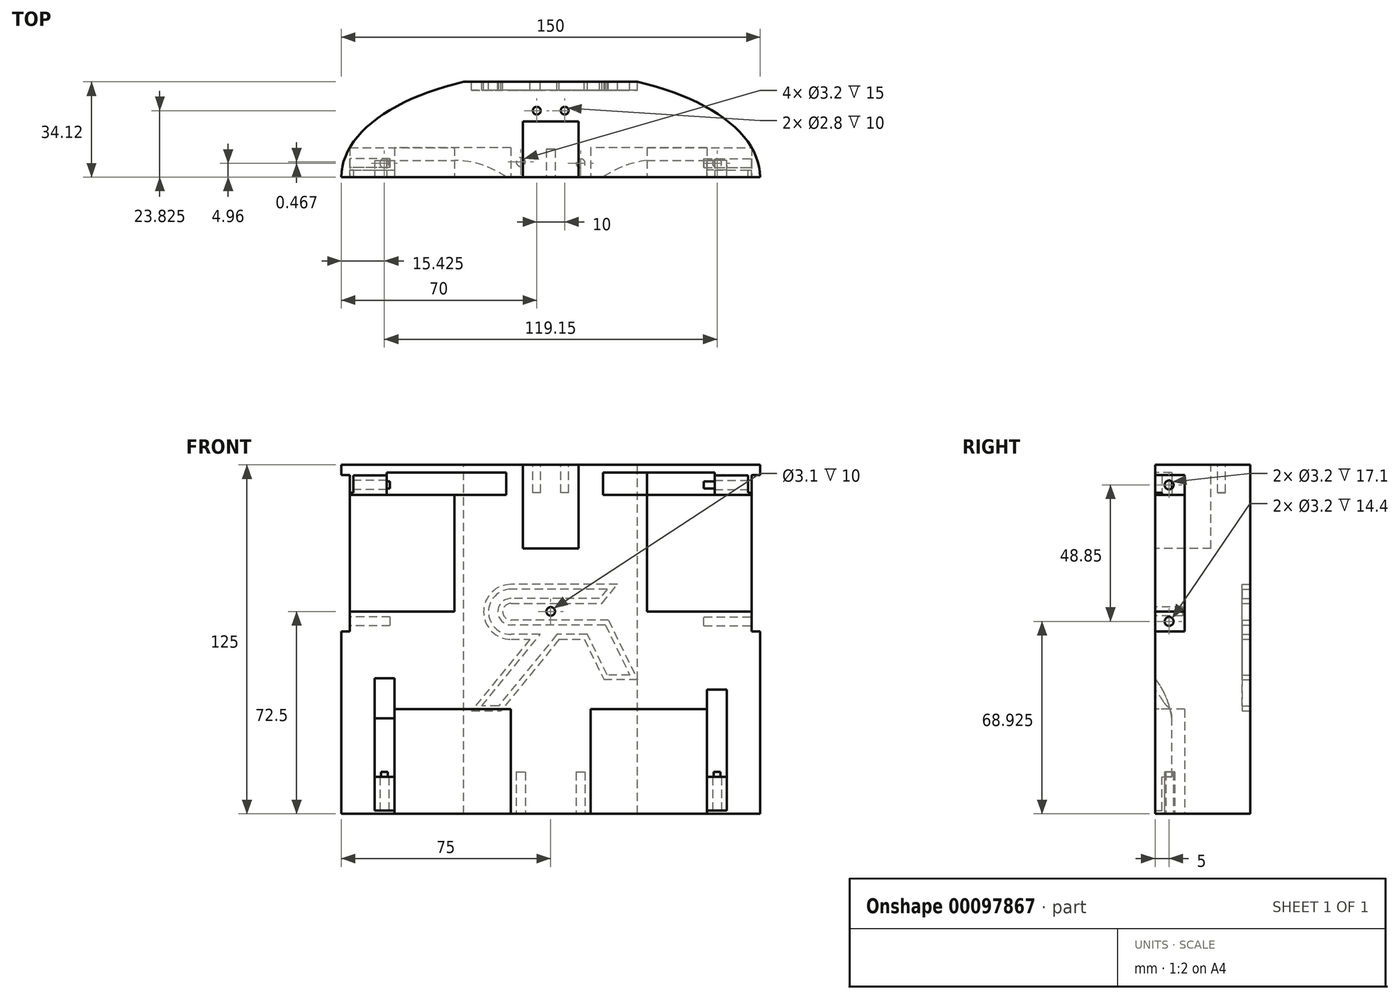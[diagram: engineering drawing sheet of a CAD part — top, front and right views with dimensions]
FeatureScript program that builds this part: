
annotation { "Feature Type Name" : "Feature", "Feature Type Description" : "" }
export const myFeature = defineFeature(function(context is Context, id is Id, definition is map)
    precondition{}
    {
        {
            var Q0;
            Q0=qCreatedBy(makeId("Top.planeOp"),FACE);
            var sketch = newSketch(context, id + "F0", { "sketchPlane" : qUnion([Q0])});
            skLineSegment(sketch, "E0.bottom", {"start": v(-150, 0) * mm, "end": v(0, 0) * mm});
            skLineSegment(sketch, "E0.top", {"start": v(-150, -75) * mm, "end": v(0, -75) * mm});
            skLineSegment(sketch, "E0.left", {"start": v(-150, 0) * mm, "end": v(-150, -75) * mm});
            skLineSegment(sketch, "E0.right", {"start": v(0, 0) * mm, "end": v(0, -75) * mm});
            skLineSegment(sketch, "E1", {"start": v(0, -37.5) * mm, "end": v(-150, -37.5) * mm});
            skPoint(sketch, "E2", {"position": v(-75, -37.5) * mm});
            skEllipse(sketch, "E3", {"center": v(-75, -37.5) * mm, "majorRadius": 75 * mm, "minorRadius": 37.5 * mm, "majorAxis": v(1, 0)});
            skSolve(sketch);
        }
        {
            var Q0;
            {var subQ0=sQuery(id+"F0.wireOp",EDGE,"E1");Q0=makeQuery(id+"F0.imprint","IMPRINT",FACE,{"disambiguationData":[TD([[makeQuery(id+"F0.imprint","IMPRINT",EDGE,{"derivedFrom":subQ0}),1.0]])]});}
            var Q1;
            {var subQ0=sQuery(id+"F0.wireOp",EDGE,"E1");Q1=makeQuery(id+"F0.imprint","IMPRINT",FACE,{"disambiguationData":[TD([[makeQuery(id+"F0.imprint","IMPRINT",EDGE,{"derivedFrom":subQ0}),-1.0]])]});}
            extrude(context, id + "F1", {"entities" : qUnion([Q0, Q1]), "depth" : 125 * mm});
        }
        {
            var Q0;
            Q0=qCreatedBy(makeId("Right.planeOp"),FACE);
            var sketch = newSketch(context, id + "F2", { "sketchPlane" : qUnion([Q0])});
            skLineSegment(sketch, "E4.bottom", {"start": v(-48.1, 114.2) * mm, "end": v(-26.9, 114.2) * mm});
            skLineSegment(sketch, "E4.top", {"start": v(-48.1, 72.5) * mm, "end": v(-26.9, 72.5) * mm});
            skLineSegment(sketch, "E4.left", {"start": v(-48.1, 114.2) * mm, "end": v(-48.1, 72.5) * mm});
            skLineSegment(sketch, "E4.right", {"start": v(-26.9, 114.2) * mm, "end": v(-26.9, 72.5) * mm});
            skPoint(sketch, "E5", {"position": v(-37.5, 125) * mm});
            skPoint(sketch, "E6", {"position": v(-37.5, 114.2) * mm});
            skLineSegment(sketch, "E7", {"start": v(-37.5, 125) * mm, "end": v(-37.5, 121.35) * mm});
            skLineSegment(sketch, "E8.bottom", {"start": v(-48.1, 113.35) * mm, "end": v(-26.9, 113.35) * mm, "construction": true});
            skLineSegment(sketch, "E8.top", {"start": v(-48.1, 73.35) * mm, "end": v(-26.9, 73.35) * mm, "construction": true});
            skLineSegment(sketch, "E8.left", {"start": v(-48.1, 113.35) * mm, "end": v(-48.1, 73.35) * mm, "construction": true});
            skLineSegment(sketch, "E8.right", {"start": v(-26.9, 113.35) * mm, "end": v(-26.9, 73.35) * mm, "construction": true});
            skPoint(sketch, "E9", {"position": v(-26.9, 93.35) * mm});
            skLineSegment(sketch, "E10.bottom", {"start": v(-48.1, 113.35) * mm, "end": v(-26.9, 113.35) * mm});
            skLineSegment(sketch, "E10.top", {"start": v(-48.1, 121.35) * mm, "end": v(-26.9, 121.35) * mm});
            skLineSegment(sketch, "E10.left", {"start": v(-48.1, 113.35) * mm, "end": v(-48.1, 121.35) * mm});
            skLineSegment(sketch, "E10.right", {"start": v(-26.9, 113.35) * mm, "end": v(-26.9, 121.35) * mm});
            skLineSegment(sketch, "E11.bottom", {"start": v(-48.1, 73.35) * mm, "end": v(-26.9, 73.35) * mm});
            skLineSegment(sketch, "E11.top", {"start": v(-48.1, 65.35) * mm, "end": v(-26.9, 65.35) * mm});
            skLineSegment(sketch, "E11.left", {"start": v(-48.1, 73.35) * mm, "end": v(-48.1, 65.35) * mm});
            skLineSegment(sketch, "E11.right", {"start": v(-26.9, 73.35) * mm, "end": v(-26.9, 65.35) * mm});
            skLineSegment(sketch, "E12", {"start": v(-37.5, 65.35) * mm, "end": v(-37.5, 0) * mm});
            skLineSegment(sketch, "E13", {"start": v(-37.5, 121.35) * mm, "end": v(-37.5, 125) * mm});
            skLineSegment(sketch, "E14.trimOffspring", {"start": v(-37.5, 114.2) * mm, "end": v(-37.5, 72.5) * mm});
            skSolve(sketch);
        }
        {
            var Q0;
            {var subQ0=sQuery(id+"F2.wireOp",EDGE,"E4.right");Q0=makeQuery(id+"F2.imprint","IMPRINT",FACE,{"disambiguationData":[TD([[makeQuery(id+"F2.imprint","IMPRINT",EDGE,{"derivedFrom":subQ0}),-1.0]])]});}
            var Q1;
            {var subQ0=sQuery(id+"F2.wireOp",EDGE,"E4.left");Q1=makeQuery(id+"F2.imprint","IMPRINT",FACE,{"disambiguationData":[TD([[makeQuery(id+"F2.imprint","IMPRINT",EDGE,{"derivedFrom":subQ0}),1.0]])]});}
            var Q2;
            {var subQ0=sQuery(id+"F2.wireOp",EDGE,"E11.left");var subQ1=sQuery(id+"F2.wireOp",EDGE,"E4.top");var subQ2=makeQuery(id+"F2.imprint","INTERSECT",VERTEX,{"derivedFrom":[subQ1,subQ0]});Q2=makeQuery(id+"F2.imprint","IMPRINT",FACE,{"disambiguationData":[TD([[makeQuery(id+"F2.imprint","IMPRINT",EDGE,{"disambiguationData":[TD([[subQ2,-1.0]])],"derivedFrom":subQ1}),1.0]])]});}
            var Q3;
            {var subQ0=sQuery(id+"F2.wireOp",EDGE,"E11.right");var subQ1=sQuery(id+"F2.wireOp",EDGE,"E4.top");var subQ2=makeQuery(id+"F2.imprint","INTERSECT",VERTEX,{"derivedFrom":[subQ1,subQ0]});Q3=makeQuery(id+"F2.imprint","IMPRINT",FACE,{"disambiguationData":[TD([[makeQuery(id+"F2.imprint","IMPRINT",EDGE,{"disambiguationData":[TD([[subQ2,1.0]])],"derivedFrom":subQ1}),1.0]])]});}
            var Q4;
            {var subQ0=sQuery(id+"F2.wireOp",EDGE,"E10.left");var subQ1=sQuery(id+"F2.wireOp",EDGE,"E4.bottom");var subQ2=makeQuery(id+"F2.imprint","INTERSECT",VERTEX,{"derivedFrom":[subQ1,subQ0]});Q4=makeQuery(id+"F2.imprint","IMPRINT",FACE,{"disambiguationData":[TD([[makeQuery(id+"F2.imprint","IMPRINT",EDGE,{"disambiguationData":[TD([[subQ2,-1.0]])],"derivedFrom":subQ1}),-1.0]])]});}
            var Q5;
            {var subQ0=sQuery(id+"F2.wireOp",EDGE,"E10.right");var subQ1=sQuery(id+"F2.wireOp",EDGE,"E4.bottom");var subQ2=makeQuery(id+"F2.imprint","INTERSECT",VERTEX,{"derivedFrom":[subQ1,subQ0]});Q5=makeQuery(id+"F2.imprint","IMPRINT",FACE,{"disambiguationData":[TD([[makeQuery(id+"F2.imprint","IMPRINT",EDGE,{"disambiguationData":[TD([[subQ2,1.0]])],"derivedFrom":subQ1}),-1.0]])]});}
            extrude(context, id + "F3", {"entities" : qUnion([Q0, Q1, Q2, Q3, Q4, Q5]), "operationType" : NewBodyOperationType.REMOVE, "oppositeDirection" : true, "depth" : 155.5 * mm});
        }
        {
            var Q0;
            Q0=makeQuery(id+"F3.boolean.opBoolean","COPY",FACE,{"derivedFrom":makeQuery(id+"F3.opExtrude","SWEPT_FACE",FACE,{"disambiguationData":[OSD([sQuery(id+"F2.wireOp",EDGE,"E4.top")])]})});
            var sketch = newSketch(context, id + "F4", { "sketchPlane" : qUnion([Q0])});
            skLineSegment(sketch, "E15", {"start": v(-3.06, -48.1) * mm, "end": v(-3.06, -26.9) * mm});
            skEllipticalArc(sketch, "E16.0", {});
            skLineSegment(sketch, "E17", {"start": v(-146.94, -48.1) * mm, "end": v(-146.94, -26.9) * mm});
            skEllipticalArc(sketch, "E18.0", {});
            const initialGuessF4  = {"E16.0": [-0.075, -0.0375, 1, 0, 0.075, 0.0375, 5.996612290444908, 0.28657301673467844], "E18.0": [-0.075, -0.0375, 1, 0, 0.075, 0.0375, 2.855019636855115, 3.428165670324471]};
            skSetInitialGuess(sketch, initialGuessF4);
            skSolve(sketch);
        }
        {
            var Q0;
            Q0=makeQuery(id+"F4.imprint","IMPRINT",FACE,{"disambiguationData":[TD([[makeQuery(id+"F4.imprint","IMPRINT",EDGE,{"derivedFrom":sQuery(id+"F4.wireOp",EDGE,"E17")}),1.0]])]});
            var Q1;
            Q1=makeQuery(id+"F4.imprint","IMPRINT",FACE,{"disambiguationData":[TD([[makeQuery(id+"F4.imprint","IMPRINT",EDGE,{"derivedFrom":sQuery(id+"F4.wireOp",EDGE,"E15")}),-1.0]])]});
            extrude(context, id + "F5", {"entities" : qUnion([Q0, Q1]), "operationType" : NewBodyOperationType.REMOVE, "oppositeDirection" : true, "depth" : 7.15 * mm});
        }
        {
            var Q0;
            Q0=makeQuery(id+"F3.boolean.opBoolean","COPY",FACE,{"derivedFrom":makeQuery(id+"F3.opExtrude","SWEPT_FACE",FACE,{"disambiguationData":[OSD([sQuery(id+"F2.wireOp",EDGE,"E4.bottom")])]})});
            var sketch = newSketch(context, id + "F6", { "sketchPlane" : qUnion([Q0])});
            skLineSegment(sketch, "E19", {"start": v(-3.06, 26.9) * mm, "end": v(-3.06, 48.1) * mm});
            skEllipticalArc(sketch, "E20.0", {});
            skLineSegment(sketch, "E21", {"start": v(-146.94, 26.9) * mm, "end": v(-146.94, 48.1) * mm});
            skEllipticalArc(sketch, "E22.0", {});
            const initialGuessF6  = {"E20.0": [-0.075, 0.0375, 1, 0, 0.075, 0.0375, 5.996612290444908, 0.28657301673467805], "E22.0": [-0.075, 0.0375, 1, 0, 0.075, 0.0375, 2.8550196368551153, 3.428165670324471]};
            skSetInitialGuess(sketch, initialGuessF6);
            skSolve(sketch);
        }
        {
            var Q0;
            Q0=makeQuery(id+"F6.imprint","IMPRINT",FACE,{"disambiguationData":[TD([[makeQuery(id+"F6.imprint","IMPRINT",EDGE,{"derivedFrom":sQuery(id+"F6.wireOp",EDGE,"E21")}),1.0]])]});
            var Q1;
            Q1=makeQuery(id+"F6.imprint","IMPRINT",FACE,{"disambiguationData":[TD([[makeQuery(id+"F6.imprint","IMPRINT",EDGE,{"derivedFrom":sQuery(id+"F6.wireOp",EDGE,"E19")}),-1.0]])]});
            extrude(context, id + "F7", {"entities" : qUnion([Q0, Q1]), "operationType" : NewBodyOperationType.REMOVE, "oppositeDirection" : true, "depth" : 7.15 * mm});
        }
        {
            var Q0;
            Q0=makeQuery(id+"F3.boolean.opBoolean","COPY",FACE,{"derivedFrom":makeQuery(id+"F3.opExtrude","SWEPT_FACE",FACE,{"disambiguationData":[OSD([sQuery(id+"F2.wireOp",EDGE,"E4.top")])]})});
            var sketch = newSketch(context, id + "F8", { "sketchPlane" : qUnion([Q0])});
            skLineSegment(sketch, "E23.bottom", {"start": v(-109.44, -26.9) * mm, "end": v(-40.56, -26.9) * mm});
            skLineSegment(sketch, "E23.top", {"start": v(-109.44, -48.1) * mm, "end": v(-40.56, -48.1) * mm});
            skLineSegment(sketch, "E23.left", {"start": v(-109.44, -26.9) * mm, "end": v(-109.44, -48.1) * mm});
            skLineSegment(sketch, "E23.right", {"start": v(-40.56, -26.9) * mm, "end": v(-40.56, -48.1) * mm});
            skSolve(sketch);
        }
        {
            var Q0;
            Q0=makeQuery(id+"F8.imprint","IMPRINT",FACE,{"disambiguationData":[TD([[makeQuery(id+"F8.imprint","IMPRINT",EDGE,{"derivedFrom":sQuery(id+"F8.wireOp",EDGE,"E23.bottom")}),-1.0]])]});
            extrude(context, id + "F9", {"entities" : qUnion([Q0]), "operationType" : NewBodyOperationType.ADD, "depth" : 46 * mm});
        }
        {
            var Q0;
            Q0=makeQuery(id+"F9.boolean.opBoolean","SPLIT",FACE,{"disambiguationData":[TD([makeQuery(id+"F7.boolean.opBoolean","COPY",FACE,{"derivedFrom":makeQuery(id+"F7.opExtrude","SWEPT_FACE",FACE,{"disambiguationData":[OSD([sQuery(id+"F6.wireOp",EDGE,"E21")])]})})])],"derivedFrom":makeQuery(id+"F3.boolean.opBoolean","COPY",FACE,{"derivedFrom":makeQuery(id+"F3.opExtrude","SWEPT_FACE",FACE,{"disambiguationData":[OSD([sQuery(id+"F2.wireOp",EDGE,"E4.bottom")])]})})});
            var sketch = newSketch(context, id + "F10", { "sketchPlane" : qUnion([Q0])});
            skLineSegment(sketch, "E24", {"start": v(-145.7, 26.9) * mm, "end": v(-145.7, 48.1) * mm, "construction": true});
            skLineSegment(sketch, "E25", {"start": v(-145.7, 37.5) * mm, "end": v(-142.91, 37.5) * mm});
            skLineSegment(sketch, "E26.bottom", {"start": v(-145.7, 35) * mm, "end": v(-4.3, 35) * mm});
            skLineSegment(sketch, "E26.top", {"start": v(-145.7, 40) * mm, "end": v(-4.3, 40) * mm});
            skLineSegment(sketch, "E26.left", {"start": v(-145.7, 35) * mm, "end": v(-145.7, 40) * mm});
            skLineSegment(sketch, "E26.right", {"start": v(-4.3, 35) * mm, "end": v(-4.3, 40) * mm});
            skLineSegment(sketch, "E27", {"start": v(-4.3, 26.9) * mm, "end": v(-4.3, 48.1) * mm, "construction": true});
            skLineSegment(sketch, "E28", {"start": v(-145.7, 37.5) * mm, "end": v(-145.7, 40) * mm});
            skLineSegment(sketch, "E29", {"start": v(-145.7, 35) * mm, "end": v(-145.7, 37.5) * mm});
            skSolve(sketch);
        }
        {
            var Q0;
            Q0=qSketchRegion(id+"F10",true);
            extrude(context, id + "F11", {"entities" : qUnion([Q0]), "operationType" : NewBodyOperationType.REMOVE, "oppositeDirection" : true, "depth" : 7 * mm});
        }
        {
            var Q0;
            Q0=makeQuery(id+"F9.boolean.opBoolean","SPLIT",FACE,{"disambiguationData":[TD([makeQuery(id+"F7.boolean.opBoolean","COPY",FACE,{"derivedFrom":makeQuery(id+"F7.opExtrude","SWEPT_FACE",FACE,{"disambiguationData":[OSD([sQuery(id+"F6.wireOp",EDGE,"E21")])]})})])],"derivedFrom":makeQuery(id+"F3.boolean.opBoolean","COPY",FACE,{"derivedFrom":makeQuery(id+"F3.opExtrude","SWEPT_FACE",FACE,{"disambiguationData":[OSD([sQuery(id+"F2.wireOp",EDGE,"E4.bottom")])]})})});
            var sketch = newSketch(context, id + "F12", { "sketchPlane" : qUnion([Q0])});
            skLineSegment(sketch, "E30.bottom", {"start": v(-133.7, 31.5) * mm, "end": v(-16.3, 31.5) * mm});
            skLineSegment(sketch, "E30.top", {"start": v(-133.7, 43.5) * mm, "end": v(-16.3, 43.5) * mm});
            skLineSegment(sketch, "E30.left", {"start": v(-133.7, 31.5) * mm, "end": v(-133.7, 43.5) * mm});
            skLineSegment(sketch, "E30.right", {"start": v(-16.3, 31.5) * mm, "end": v(-16.3, 43.5) * mm});
            skLineSegment(sketch, "E31", {"start": v(-133.7, 35) * mm, "end": v(-133.7, 40) * mm});
            skPoint(sketch, "E32", {"position": v(-133.7, 37.5) * mm});
            skLineSegment(sketch, "E33", {"start": v(-16.3, 35) * mm, "end": v(-16.3, 40) * mm});
            skPoint(sketch, "E34", {"position": v(-16.3, 37.5) * mm});
            skSolve(sketch);
        }
        {
            var Q0;
            Q0=qSketchRegion(id+"F12",true);
            extrude(context, id + "F13", {"entities" : qUnion([Q0]), "operationType" : NewBodyOperationType.REMOVE, "oppositeDirection" : true, "depth" : 8 * mm});
        }
        {
            var Q0;
            Q0=makeQuery(id+"F9.boolean.opBoolean","SPLIT",FACE,{"disambiguationData":[TD([makeQuery(id+"F7.boolean.opBoolean","COPY",FACE,{"derivedFrom":makeQuery(id+"F7.opExtrude","SWEPT_FACE",FACE,{"disambiguationData":[OSD([sQuery(id+"F6.wireOp",EDGE,"E21")])]})})])],"derivedFrom":makeQuery(id+"F3.boolean.opBoolean","COPY",FACE,{"derivedFrom":makeQuery(id+"F3.opExtrude","SWEPT_FACE",FACE,{"disambiguationData":[OSD([sQuery(id+"F2.wireOp",EDGE,"E4.bottom")])]})})});
            var sketch = newSketch(context, id + "F14", { "sketchPlane" : qUnion([Q0])});
            skArc(sketch, "E35", {"start": v(-109.44, 31.5) * mm, "mid": v(-83.34, 45.45) * mm, "end": v(-80.45, 74.9) * mm});
            skArc(sketch, "E36", {"start": v(-109.44, 43.5) * mm, "mid": v(-91.99, 53.74) * mm, "end": v(-92.41, 73.98) * mm});
            skEllipticalArc(sketch, "E37.0", {});
            skLineSegment(sketch, "E38", {"start": v(-109.44, 31.5) * mm, "end": v(-109.44, 43.5) * mm});
            skArc(sketch, "E39", {"start": v(-69.55, 74.9) * mm, "mid": v(-65.03, 46.53) * mm, "end": v(-40.56, 31.5) * mm});
            skArc(sketch, "E40", {"start": v(-57.59, 73.98) * mm, "mid": v(-55.43, 55.19) * mm, "end": v(-40.56, 43.5) * mm});
            skEllipticalArc(sketch, "E41.0", {});
            skLineSegment(sketch, "E42", {"start": v(-40.56, 31.5) * mm, "end": v(-40.56, 43.5) * mm});
            skLineSegment(sketch, "E43", {"start": v(-75, 37.5) * mm, "end": v(-75, 74.9) * mm, "construction": true});
            skLineSegment(sketch, "E44", {"start": v(-69.55, 74.9) * mm, "end": v(-75, 74.9) * mm, "construction": true});
            skLineSegment(sketch, "E45", {"start": v(-80.45, 74.9) * mm, "end": v(-75, 74.9) * mm, "construction": true});
            const initialGuessF14  = {"E37.0": [-0.075, 0.0375, 1, 0, 0.075, 0.0375, 1.6434997456011395, 1.8050969396186902], "E41.0": [-0.075, 0.0375, 1, 0, 0.075, 0.0375, 1.3364957139711027, 1.4980929079886538], "E37.0": [-0.075, 0.0375, 1, 0, 0.075, 0.0375, 1.6434997456011395, 1.8050969396186902]};
            skSetInitialGuess(sketch, initialGuessF14);
            skSolve(sketch);
        }
        {
            var Q0;
            Q0=qSketchRegion(id+"F14",true);
            extrude(context, id + "F15", {"entities" : qUnion([Q0]), "operationType" : NewBodyOperationType.REMOVE, "oppositeDirection" : true, "depth" : 8 * mm});
        }
        {
            var Q0;
            Q0=makeQuery(id+"F15.boolean.opBoolean","MERGE",FACE,{"derivedFrom":[makeQuery(id+"F13.boolean.opBoolean","MERGE",FACE,{"derivedFrom":[makeQuery(id+"F11.boolean.opBoolean","COPY",FACE,{"derivedFrom":makeQuery(id+"F11.opExtrude","CAP_FACE",FACE,{"disambiguationData":[OSD([sQuery(id+"F10.wireOp",EDGE,"E26.bottom"),sQuery(id+"F10.wireOp",EDGE,"E26.top"),sQuery(id+"F10.wireOp",EDGE,"E26.right"),sQuery(id+"F10.wireOp",EDGE,"E28"),sQuery(id+"F10.wireOp",EDGE,"E29")])],"isStart":true})}),makeQuery(id+"F13.opExtrude","CAP_FACE",FACE,{"disambiguationData":[OSD([sQuery(id+"F12.wireOp",EDGE,"E30.bottom"),sQuery(id+"F12.wireOp",EDGE,"E30.top"),sQuery(id+"F12.wireOp",EDGE,"E30.left"),sQuery(id+"F12.wireOp",EDGE,"E30.right"),sQuery(id+"F12.wireOp",EDGE,"E31"),sQuery(id+"F12.wireOp",EDGE,"E33")])],"isStart":true})]}),makeQuery(id+"F15.opExtrude","CAP_FACE",FACE,{"disambiguationData":[OSD([sQuery(id+"F14.wireOp",EDGE,"E35"),sQuery(id+"F14.wireOp",EDGE,"E36"),sQuery(id+"F14.wireOp",EDGE,"E38"),sQuery(id+"F14.wireOp",EDGE,"E37.0")])],"isStart":true}),makeQuery(id+"F15.opExtrude","CAP_FACE",FACE,{"disambiguationData":[OSD([sQuery(id+"F14.wireOp",EDGE,"E39"),sQuery(id+"F14.wireOp",EDGE,"E40"),sQuery(id+"F14.wireOp",EDGE,"E41.0"),sQuery(id+"F14.wireOp",EDGE,"E42")])],"isStart":true})]});
            var sketch = newSketch(context, id + "F16", { "sketchPlane" : qUnion([Q0])});
            skArc(sketch, "E46.0", {"start": v(-84.76, -43.5) * mm, "mid": v(-78.35, -58.62) * mm, "end": v(-80.45, -74.9) * mm, "construction": true});
            skArc(sketch, "E46.1", {"start": v(-69.55, -74.9) * mm, "mid": v(-70.05, -58.36) * mm, "end": v(-62.76, -43.5) * mm, "construction": true});
            skLineSegment(sketch, "E47", {"start": v(-62.76, -43.5) * mm, "end": v(-84.76, -43.5) * mm});
            skArc(sketch, "E48", {"start": v(-84.76, -43.5) * mm, "mid": v(-95.72, -34.66) * mm, "end": v(-109.44, -31.5) * mm});
            skArc(sketch, "E49", {"start": v(-40.56, -31.5) * mm, "mid": v(-52.8, -35.39) * mm, "end": v(-62.76, -43.5) * mm});
            skLineSegment(sketch, "E50", {"start": v(-109.44, -31.5) * mm, "end": v(-40.56, -31.5) * mm});
            skSolve(sketch);
        }
        {
            var Q0;
            Q0=qSketchRegion(id+"F16",true);
            extrude(context, id + "F17", {"entities" : qUnion([Q0]), "operationType" : NewBodyOperationType.ADD, "depth" : 9.4 * mm});
        }
        {
            var Q0;
            Q0=makeQuery(id+"F7.boolean.opBoolean","COPY",FACE,{"derivedFrom":makeQuery(id+"F7.opExtrude","SWEPT_FACE",FACE,{"disambiguationData":[OSD([sQuery(id+"F6.wireOp",EDGE,"E19")])]})});
            var sketch = newSketch(context, id + "F18", { "sketchPlane" : qUnion([Q0])});
            skLineSegment(sketch, "E51", {"start": v(-48.1, 117.77) * mm, "end": v(-26.9, 117.77) * mm, "construction": true});
            skCircle(sketch, "E52", {"center": v(-42.5, 117.78) * mm, "radius": 1.6 * mm});
            skCircle(sketch, "E53", {"center": v(-32.5, 117.78) * mm, "radius": 1.6 * mm});
            skLineSegment(sketch, "E54", {"start": v(-32.5, 117.77) * mm, "end": v(-42.5, 117.77) * mm});
            skPoint(sketch, "E55", {"position": v(-37.5, 117.77) * mm});
            skLineSegment(sketch, "E56", {"start": v(-26.9, 68.92) * mm, "end": v(-48.1, 68.92) * mm, "construction": true});
            skCircle(sketch, "E57", {"center": v(-32.5, 68.92) * mm, "radius": 1.6 * mm});
            skCircle(sketch, "E58", {"center": v(-42.5, 68.92) * mm, "radius": 1.6 * mm});
            skPoint(sketch, "E59", {"position": v(-37.5, 68.92) * mm});
            skLineSegment(sketch, "E60", {"start": v(-32.5, 68.92) * mm, "end": v(-42.5, 68.92) * mm});
            skSolve(sketch);
        }
        {
            var Q0;
            Q0=qSketchRegion(id+"F18",true);
            extrude(context, id + "F19", {"entities" : qUnion([Q0]), "operationType" : NewBodyOperationType.REMOVE, "oppositeDirection" : true, "depth" : 17.1 * mm});
        }
        {
            var Q0;
            Q0=makeQuery(id+"F7.boolean.opBoolean","COPY",FACE,{"derivedFrom":makeQuery(id+"F7.opExtrude","SWEPT_FACE",FACE,{"disambiguationData":[OSD([sQuery(id+"F6.wireOp",EDGE,"E21")])]})});
            var sketch = newSketch(context, id + "F20", { "sketchPlane" : qUnion([Q0])});
            skCircle(sketch, "E61.0", {"center": v(32.5, 68.92) * mm, "radius": 1.6 * mm});
            skCircle(sketch, "E61.1", {"center": v(42.5, 68.92) * mm, "radius": 1.6 * mm});
            skCircle(sketch, "E61.2", {"center": v(42.5, 117.78) * mm, "radius": 1.6 * mm});
            skCircle(sketch, "E61.3", {"center": v(32.5, 117.78) * mm, "radius": 1.6 * mm});
            skSolve(sketch);
        }
        {
            var Q0;
            Q0=qSketchRegion(id+"F20",true);
            extrude(context, id + "F21", {"entities" : qUnion([Q0]), "operationType" : NewBodyOperationType.REMOVE, "oppositeDirection" : true, "depth" : 14.4 * mm});
        }
        {
            var Q0;
            Q0=makeQuery(id+"F1.opExtrude","CAP_FACE",FACE,{"disambiguationData":[OSD([sQuery(id+"F0.wireOp",EDGE,"E3")])],"isStart":true});
            var sketch = newSketch(context, id + "F22", { "sketchPlane" : qUnion([Q0])});
            skLineSegment(sketch, "E62", {"start": v(-75, 0) * mm, "end": v(-75, 75) * mm, "construction": true});
            skLineSegment(sketch, "E63.bottom", {"start": v(-19, 26.9) * mm, "end": v(-60.7, 26.9) * mm});
            skLineSegment(sketch, "E63.top", {"start": v(-19, 48.1) * mm, "end": v(-60.7, 48.1) * mm});
            skLineSegment(sketch, "E63.left", {"start": v(-19, 26.9) * mm, "end": v(-19, 48.1) * mm});
            skLineSegment(sketch, "E63.right", {"start": v(-60.7, 26.9) * mm, "end": v(-60.7, 48.1) * mm});
            skLineSegment(sketch, "E64.bottom", {"start": v(-89.3, 26.9) * mm, "end": v(-131, 26.9) * mm});
            skLineSegment(sketch, "E64.top", {"start": v(-89.3, 48.1) * mm, "end": v(-131, 48.1) * mm});
            skLineSegment(sketch, "E64.left", {"start": v(-89.3, 26.9) * mm, "end": v(-89.3, 48.1) * mm});
            skLineSegment(sketch, "E64.right", {"start": v(-131, 26.9) * mm, "end": v(-131, 48.1) * mm});
            skLineSegment(sketch, "E65", {"start": v(-89.3, 37.5) * mm, "end": v(-75, 37.5) * mm});
            skLineSegment(sketch, "E66", {"start": v(-75, 37.5) * mm, "end": v(-60.7, 37.5) * mm});
            skLineSegment(sketch, "E67", {"start": v(-60.7, 37.5) * mm, "end": v(-75, 37.5) * mm, "construction": true});
            skLineSegment(sketch, "E68", {"start": v(-89.3, 37.5) * mm, "end": v(-75, 37.5) * mm, "construction": true});
            skLineSegment(sketch, "E69.bottom", {"start": v(-19.85, 26.9) * mm, "end": v(-59.85, 26.9) * mm});
            skLineSegment(sketch, "E69.top", {"start": v(-19.85, 48.1) * mm, "end": v(-59.85, 48.1) * mm});
            skPoint(sketch, "E70", {"position": v(-39.85, 26.9) * mm});
            skLineSegment(sketch, "E71.bottom", {"start": v(-19.85, 26.9) * mm, "end": v(-11.85, 26.9) * mm});
            skLineSegment(sketch, "E71.top", {"start": v(-19.85, 48.1) * mm, "end": v(-11.85, 48.1) * mm});
            skLineSegment(sketch, "E71.right", {"start": v(-11.85, 26.9) * mm, "end": v(-11.85, 48.1) * mm});
            skLineSegment(sketch, "E72.bottom", {"start": v(-60.7, 48.1) * mm, "end": v(-67.85, 48.1) * mm});
            skLineSegment(sketch, "E72.top", {"start": v(-60.7, 26.9) * mm, "end": v(-67.85, 26.9) * mm});
            skLineSegment(sketch, "E72.left", {"start": v(-60.7, 48.1) * mm, "end": v(-60.7, 26.9) * mm});
            skLineSegment(sketch, "E72.right", {"start": v(-67.85, 48.1) * mm, "end": v(-67.85, 26.9) * mm});
            skPoint(sketch, "E73.oppositeSnap0", {"position": v(-82.15, 37.5) * mm});
            skLineSegment(sketch, "E73.bottom", {"start": v(-89.3, 26.9) * mm, "end": v(-82.15, 26.9) * mm});
            skLineSegment(sketch, "E73.top", {"start": v(-89.3, 48.1) * mm, "end": v(-82.15, 48.1) * mm});
            skLineSegment(sketch, "E73.right", {"start": v(-82.15, 26.9) * mm, "end": v(-82.15, 48.1) * mm});
            skLineSegment(sketch, "E74.bottom", {"start": v(-131, 26.9) * mm, "end": v(-138.15, 26.9) * mm});
            skLineSegment(sketch, "E74.top", {"start": v(-131, 48.1) * mm, "end": v(-138.15, 48.1) * mm});
            skLineSegment(sketch, "E74.right", {"start": v(-138.15, 26.9) * mm, "end": v(-138.15, 48.1) * mm});
            skLineSegment(sketch, "E75.bottom", {"start": v(-90.15, 26.9) * mm, "end": v(-130.15, 26.9) * mm});
            skLineSegment(sketch, "E75.top", {"start": v(-90.15, 48.1) * mm, "end": v(-130.15, 48.1) * mm});
            skPoint(sketch, "E76", {"position": v(-110.15, 26.9) * mm});
            skPoint(sketch, "E77", {"position": v(-67.85, 37.5) * mm});
            skLineSegment(sketch, "E78", {"start": v(-19, 26.9) * mm, "end": v(-11.85, 26.9) * mm});
            skLineSegment(sketch, "E79", {"start": v(-19, 48.1) * mm, "end": v(-11.85, 48.1) * mm});
            skCircle(sketch, "E80", {"center": v(-15.42, 32.53) * mm, "radius": 1.6 * mm});
            skCircle(sketch, "E81", {"center": v(-15.42, 42.53) * mm, "radius": 1.6 * mm});
            skCircle(sketch, "E82", {"center": v(-64.27, 32.54) * mm, "radius": 1.6 * mm});
            skCircle(sketch, "E83", {"center": v(-64.27, 42.54) * mm, "radius": 1.6 * mm});
            skCircle(sketch, "E84", {"center": v(-85.73, 42.07) * mm, "radius": 1.6 * mm});
            skCircle(sketch, "E85", {"center": v(-85.73, 32.07) * mm, "radius": 1.6 * mm});
            skCircle(sketch, "E86", {"center": v(-134.57, 32.51) * mm, "radius": 1.6 * mm});
            skCircle(sketch, "E87", {"center": v(-134.57, 42.51) * mm, "radius": 1.6 * mm});
            skLineSegment(sketch, "E88", {"start": v(-138.15, 37.5) * mm, "end": v(-11.85, 37.5) * mm, "construction": true});
            skLineSegment(sketch, "E89", {"start": v(-15.42, 32.53) * mm, "end": v(-15.42, 42.53) * mm});
            skLineSegment(sketch, "E90", {"start": v(-64.27, 32.54) * mm, "end": v(-64.27, 42.54) * mm});
            skLineSegment(sketch, "E91", {"start": v(-85.73, 32.07) * mm, "end": v(-85.73, 42.07) * mm});
            skLineSegment(sketch, "E92", {"start": v(-134.57, 32.51) * mm, "end": v(-134.57, 42.51) * mm});
            skSolve(sketch);
        }
        {
            var Q0;
            {var subQ0=sQuery(id+"F22.wireOp",EDGE,"E63.left");Q0=makeQuery(id+"F22.imprint","IMPRINT",FACE,{"disambiguationData":[TD([[makeQuery(id+"F22.imprint","IMPRINT",EDGE,{"derivedFrom":subQ0}),1.0]])]});}
            var Q1;
            {var subQ1=sQuery(id+"F22.wireOp",EDGE,"E63.bottom");Q1=makeQuery(id+"F22.imprint","IMPRINT",FACE,{"disambiguationData":[TD([[makeQuery(id+"F22.imprint","IMPRINT",EDGE,{"derivedFrom":subQ1}),-1.0]])]});}
            var Q2;
            {var subQ0=sQuery(id+"F22.wireOp",EDGE,"E64.right");Q2=makeQuery(id+"F22.imprint","IMPRINT",FACE,{"disambiguationData":[TD([[makeQuery(id+"F22.imprint","IMPRINT",EDGE,{"derivedFrom":subQ0}),-1.0]])]});}
            extrude(context, id + "F23", {"entities" : qUnion([Q0, Q1, Q2]), "operationType" : NewBodyOperationType.REMOVE, "oppositeDirection" : true, "depth" : 37.5 * mm});
        }
        {
            var Q0;
            Q0=makeQuery(id+"F22.imprint","IMPRINT",FACE,{"disambiguationData":[TD([[makeQuery(id+"F22.imprint","IMPRINT",EDGE,{"derivedFrom":sQuery(id+"F22.wireOp",EDGE,"E80")}),1.0]])]});
            var Q1;
            Q1=makeQuery(id+"F22.imprint","IMPRINT",FACE,{"disambiguationData":[TD([[makeQuery(id+"F22.imprint","IMPRINT",EDGE,{"derivedFrom":sQuery(id+"F22.wireOp",EDGE,"E81")}),1.0]])]});
            var Q2;
            Q2=makeQuery(id+"F22.imprint","IMPRINT",FACE,{"disambiguationData":[TD([[makeQuery(id+"F22.imprint","IMPRINT",EDGE,{"derivedFrom":sQuery(id+"F22.wireOp",EDGE,"E82")}),1.0]])]});
            var Q3;
            Q3=makeQuery(id+"F22.imprint","IMPRINT",FACE,{"disambiguationData":[TD([[makeQuery(id+"F22.imprint","IMPRINT",EDGE,{"derivedFrom":sQuery(id+"F22.wireOp",EDGE,"E83")}),1.0]])]});
            var Q4;
            Q4=makeQuery(id+"F22.imprint","IMPRINT",FACE,{"disambiguationData":[TD([[makeQuery(id+"F22.imprint","IMPRINT",EDGE,{"derivedFrom":sQuery(id+"F22.wireOp",EDGE,"E85")}),1.0]])]});
            var Q5;
            Q5=makeQuery(id+"F22.imprint","IMPRINT",FACE,{"disambiguationData":[TD([[makeQuery(id+"F22.imprint","IMPRINT",EDGE,{"derivedFrom":sQuery(id+"F22.wireOp",EDGE,"E84")}),1.0]])]});
            var Q6;
            Q6=makeQuery(id+"F22.imprint","IMPRINT",FACE,{"disambiguationData":[TD([[makeQuery(id+"F22.imprint","IMPRINT",EDGE,{"derivedFrom":sQuery(id+"F22.wireOp",EDGE,"E86")}),1.0]])]});
            var Q7;
            Q7=makeQuery(id+"F22.imprint","IMPRINT",FACE,{"disambiguationData":[TD([[makeQuery(id+"F22.imprint","IMPRINT",EDGE,{"derivedFrom":sQuery(id+"F22.wireOp",EDGE,"E87")}),1.0]])]});
            extrude(context, id + "F24", {"entities" : qUnion([Q0, Q1, Q2, Q3, Q4, Q5, Q6, Q7]), "operationType" : NewBodyOperationType.REMOVE, "oppositeDirection" : true, "depth" : 15 * mm});
        }
        {
            var Q0;
            Q0=makeQuery(id+"F23.boolean.opBoolean","COPY",FACE,{"derivedFrom":makeQuery(id+"F23.opExtrude","SWEPT_FACE",FACE,{"disambiguationData":[OSD([sQuery(id+"F22.wireOp",EDGE,"E64.right")])]})});
            var sketch = newSketch(context, id + "F25", { "sketchPlane" : qUnion([Q0])});
            skLineSegment(sketch, "E93.bottom", {"start": v(-35, 1.25) * mm, "end": v(-40, 1.25) * mm});
            skLineSegment(sketch, "E93.left", {"start": v(-35, 1.25) * mm, "end": v(-35, 13.25) * mm});
            skLineSegment(sketch, "E93.right", {"start": v(-40, 1.25) * mm, "end": v(-40, 13.25) * mm});
            skLineSegment(sketch, "E94", {"start": v(-37.5, 0) * mm, "end": v(-37.5, 13.25) * mm, "construction": true});
            skLineSegment(sketch, "E95", {"start": v(-37.5, 1.25) * mm, "end": v(-35, 1.25) * mm});
            skPoint(sketch, "E95.startSnap0", {"position": v(-37.5, 1.25) * mm});
            skLineSegment(sketch, "E96", {"start": v(-37.5, 1.25) * mm, "end": v(-40, 1.25) * mm});
            skPoint(sketch, "E97", {"position": v(-37.5, 31.05) * mm});
            skLineSegment(sketch, "E98.bottom", {"start": v(-31.5, 13.25) * mm, "end": v(-35, 13.25) * mm});
            skLineSegment(sketch, "E98.left", {"start": v(-31.5, 13.25) * mm, "end": v(-31.5, 34.22) * mm});
            skLineSegment(sketch, "E98.right", {"start": v(-43.5, 13.25) * mm, "end": v(-43.5, 34.22) * mm});
            skPoint(sketch, "E99.trimOffspring.end.orphan", {"position": v(-37.5, 32.45) * mm});
            skPoint(sketch, "E100.start.orphan", {"position": v(-40, 31.05) * mm});
            skPoint(sketch, "E93.top.start.orphan", {"position": v(-35, 31.05) * mm});
            skLineSegment(sketch, "E101.trimOffspring", {"start": v(-40, 13.25) * mm, "end": v(-43.5, 13.25) * mm});
            skLineSegment(sketch, "E102", {"start": v(-40, 13.25) * mm, "end": v(-35, 13.25) * mm});
            skLineSegment(sketch, "E103", {"start": v(-43.5, 13.25) * mm, "end": v(-31.5, 13.25) * mm});
            skLineSegment(sketch, "E104", {"start": v(-37.5, 34.22) * mm, "end": v(-37.5, 13.25) * mm});
            skArc(sketch, "E105", {"start": v(-43.5, 34.22) * mm, "mid": v(-54.18, 46.6) * mm, "end": v(-70.51, 47.22) * mm});
            skArc(sketch, "E106", {"start": v(-31.5, 34.22) * mm, "mid": v(-45.26, 55.7) * mm, "end": v(-70.51, 59.22) * mm});
            skLineSegment(sketch, "E107", {"start": v(-43.5, 34.22) * mm, "end": v(-31.5, 34.22) * mm});
            skLineSegment(sketch, "E108", {"start": v(-70.51, 59.22) * mm, "end": v(-70.51, 47.22) * mm});
            skPoint(sketch, "E109.orphan", {"position": v(-31.5, 37.5) * mm});
            skPoint(sketch, "E110.orphan", {"position": v(-37.5, 37.5) * mm});
            skPoint(sketch, "E98.top.end.orphan", {"position": v(-43.5, 37.5) * mm});
            skSolve(sketch);
        }
        {
            var Q0;
            Q0=qSketchRegion(id+"F25",true);
            extrude(context, id + "F26", {"entities" : qUnion([Q0]), "operationType" : NewBodyOperationType.REMOVE, "oppositeDirection" : true, "depth" : 7 * mm});
        }
        {
            var Q0;
            Q0=makeQuery(id+"F23.boolean.opBoolean","COPY",FACE,{"derivedFrom":makeQuery(id+"F23.opExtrude","SWEPT_FACE",FACE,{"disambiguationData":[OSD([sQuery(id+"F22.wireOp",EDGE,"E63.left")])]})});
            var sketch = newSketch(context, id + "F27", { "sketchPlane" : qUnion([Q0])});
            skLineSegment(sketch, "E111.0.2", {"start": v(43.5, 34.22) * mm, "end": v(43.5, 13.25) * mm});
            skLineSegment(sketch, "E111.0.3", {"start": v(43.5, 13.25) * mm, "end": v(40, 13.25) * mm});
            skLineSegment(sketch, "E111.0.4", {"start": v(40, 13.25) * mm, "end": v(40, 1.25) * mm});
            skLineSegment(sketch, "E111.0.5", {"start": v(40, 1.25) * mm, "end": v(35, 1.25) * mm});
            skLineSegment(sketch, "E111.0.6", {"start": v(35, 1.25) * mm, "end": v(35, 13.25) * mm});
            skLineSegment(sketch, "E111.0.7", {"start": v(35, 13.25) * mm, "end": v(31.5, 13.25) * mm});
            skLineSegment(sketch, "E111.0.8", {"start": v(31.5, 13.25) * mm, "end": v(31.5, 34.22) * mm});
            skLineSegment(sketch, "E112", {"start": v(57.85, 60.27) * mm, "end": v(57.85, 47.95) * mm});
            skArc(sketch, "E113", {"start": v(57.85, 60.27) * mm, "mid": v(39.24, 52.75) * mm, "end": v(31.5, 34.22) * mm});
            skArc(sketch, "E114", {"start": v(57.85, 47.95) * mm, "mid": v(47.74, 44.15) * mm, "end": v(43.5, 34.22) * mm});
            skSolve(sketch);
        }
        {
            var Q0;
            {var subQ0=sQuery(id+"F27.wireOp",EDGE,"E111.0.2");Q0=makeQuery(id+"F27.imprint","IMPRINT",FACE,{"disambiguationData":[TD([[makeQuery(id+"F27.imprint","IMPRINT",EDGE,{"derivedFrom":subQ0}),-1.0]])]});}
            extrude(context, id + "F28", {"entities" : qUnion([Q0]), "operationType" : NewBodyOperationType.REMOVE, "oppositeDirection" : true, "depth" : 7 * mm});
        }
        {
            var Q0;
            Q0=makeQuery(id+"F23.boolean.opBoolean","COPY",FACE,{"derivedFrom":makeQuery(id+"F23.opExtrude","SWEPT_FACE",FACE,{"disambiguationData":[OSD([sQuery(id+"F22.wireOp",EDGE,"E63.left")])]})});
            var sketch = newSketch(context, id + "F29", { "sketchPlane" : qUnion([Q0])});
            skArc(sketch, "E115", {"start": v(80.51, 59.28) * mm, "mid": v(51.36, 55.84) * mm, "end": v(31.5, 34.22) * mm});
            skArc(sketch, "E116", {"start": v(82.64, 47.28) * mm, "mid": v(60.63, 48.07) * mm, "end": v(43.5, 34.22) * mm});
            skLineSegment(sketch, "E117", {"start": v(80.51, 59.28) * mm, "end": v(82.64, 47.28) * mm});
            skPoint(sketch, "E118.0", {"position": v(31.5, 34.22) * mm});
            skPoint(sketch, "E118.1", {"position": v(43.5, 34.22) * mm});
            skLineSegment(sketch, "E119", {"start": v(31.5, 34.22) * mm, "end": v(43.5, 34.22) * mm});
            skSolve(sketch);
        }
        {
            var Q0;
            Q0=qSketchRegion(id+"F29",true);
            extrude(context, id + "F30", {"entities" : qUnion([Q0]), "operationType" : NewBodyOperationType.REMOVE, "oppositeDirection" : true, "depth" : 7 * mm});
        }
        {
            var Q0;
            Q0=qCreatedBy(makeId("Right.planeOp"),FACE);
            var sketch = newSketch(context, id + "F31", { "sketchPlane" : qUnion([Q0])});
            skLineSegment(sketch, "E120.bottom", {"start": v(-37.5, 159.6) * mm, "end": v(-92.54, 159.6) * mm});
            skLineSegment(sketch, "E120.top", {"start": v(-37.5, -19.85) * mm, "end": v(-92.54, -19.85) * mm});
            skLineSegment(sketch, "E120.left", {"start": v(-37.5, 159.6) * mm, "end": v(-37.5, -19.85) * mm});
            skLineSegment(sketch, "E120.right", {"start": v(-92.54, 159.6) * mm, "end": v(-92.54, -19.85) * mm});
            skSolve(sketch);
        }
        {
            var Q0;
            Q0 = qSketchRegion(id + "F31", true);
            extrude(context, id + "F32", {"entities" : qUnion([Q0]), "operationType" : NewBodyOperationType.REMOVE, "oppositeDirection" : true, "depth" : 197 * mm});
        }
        {
            var Q0;
            Q0=makeQuery(id+"F32.boolean.opBoolean","COPY",FACE,{"derivedFrom":makeQuery(id+"F32.opExtrude","SWEPT_FACE",FACE,{"disambiguationData":[OSD([sQuery(id+"F31.wireOp",EDGE,"E120.left")])]})});
            var sketch = newSketch(context, id + "F33", { "sketchPlane" : qUnion([Q0])});
            skLineSegment(sketch, "E121", {"start": v(-40.56, 72.5) * mm, "end": v(-109.44, 72.5) * mm});
            skCircle(sketch, "E122", {"center": v(-75, 72.5) * mm, "radius": 1.55 * mm});
            skLineSegment(sketch, "E123", {"start": v(-75, 123.57) * mm, "end": v(-75, -4.49) * mm, "construction": true});
            skSolve(sketch);
        }
        {
            var Q0;
            Q0 = qSketchRegion(id + "F33", true);
            extrude(context, id + "F34", {"entities" : qUnion([Q0]), "operationType" : NewBodyOperationType.REMOVE, "oppositeDirection" : true, "depth" : 10 * mm});
        }
        {
            var Q0;
            {var subQ0=sQuery(id+"F22.wireOp",EDGE,"E63.left");Q0=makeQuery(id+"F30.boolean.opBoolean","INTERSECT",EDGE,{"derivedFrom":[makeQuery(id+"F28.boolean.opBoolean","MERGE",FACE,{"derivedFrom":[makeQuery(id+"F23.boolean.opBoolean","COPY",FACE,{"derivedFrom":makeQuery(id+"F23.opExtrude","CAP_FACE",FACE,{"disambiguationData":[OSD([sQuery(id+"F22.wireOp",EDGE,"E63.bottom"),sQuery(id+"F22.wireOp",EDGE,"E63.top"),subQ0,sQuery(id+"F22.wireOp",EDGE,"E69.bottom"),sQuery(id+"F22.wireOp",EDGE,"E69.top"),sQuery(id+"F22.wireOp",EDGE,"E71.bottom"),sQuery(id+"F22.wireOp",EDGE,"E71.top"),sQuery(id+"F22.wireOp",EDGE,"E72.left")])],"isStart":false})}),makeQuery(id+"F28.opExtrude","SWEPT_FACE",FACE,{"disambiguationData":[OSD([subQ0])]})]}),makeQuery(id+"F30.opExtrude","SWEPT_FACE",FACE,{"disambiguationData":[OSD([sQuery(id+"F29.wireOp",EDGE,"E115")])]})]});}
            fillet(context, id + "F35", {"entities" : qUnion([Q0]), "radius" : 5 * mm, "tangentPropagation" : true, "allowEdgeOverflow" : false});
        }
        {
            var Q0;
            {var subQ0=sQuery(id+"F22.wireOp",EDGE,"E63.left");Q0=makeQuery(id+"F35.opFillet","BLEND_EDGE",EDGE,{"blendedFrom":[makeQuery(id+"F30.boolean.opBoolean","INTERSECT",EDGE,{"derivedFrom":[makeQuery(id+"F28.boolean.opBoolean","MERGE",FACE,{"derivedFrom":[makeQuery(id+"F23.boolean.opBoolean","COPY",FACE,{"derivedFrom":makeQuery(id+"F23.opExtrude","CAP_FACE",FACE,{"disambiguationData":[OSD([sQuery(id+"F22.wireOp",EDGE,"E63.bottom"),sQuery(id+"F22.wireOp",EDGE,"E63.top"),subQ0,sQuery(id+"F22.wireOp",EDGE,"E69.bottom"),sQuery(id+"F22.wireOp",EDGE,"E69.top"),sQuery(id+"F22.wireOp",EDGE,"E71.bottom"),sQuery(id+"F22.wireOp",EDGE,"E71.top"),sQuery(id+"F22.wireOp",EDGE,"E72.left")])],"isStart":false})}),makeQuery(id+"F28.opExtrude","SWEPT_FACE",FACE,{"disambiguationData":[OSD([subQ0])]})]}),makeQuery(id+"F30.opExtrude","SWEPT_FACE",FACE,{"disambiguationData":[OSD([sQuery(id+"F29.wireOp",EDGE,"E115")])]})]}),makeQuery(id+"F28.boolean.opBoolean","COPY",FACE,{"derivedFrom":makeQuery(id+"F28.opExtrude","SWEPT_FACE",FACE,{"disambiguationData":[OSD([sQuery(id+"F27.wireOp",EDGE,"E113")])]})})],"blendedInto":[makeQuery(id+"F28.boolean.opBoolean","COPY",FACE,{"derivedFrom":makeQuery(id+"F28.opExtrude","SWEPT_FACE",FACE,{"disambiguationData":[OSD([sQuery(id+"F27.wireOp",EDGE,"E113")])]})})]});}
            fillet(context, id + "F47", {"entities" : qUnion([Q0]), "radius" : 5 * mm, "tangentPropagation" : true, "allowEdgeOverflow" : false});
        }
        {
            var Q0;
            Q0=makeQuery(id+"F7.boolean.opBoolean","COPY",FACE,{"derivedFrom":makeQuery(id+"F7.opExtrude","SWEPT_FACE",FACE,{"disambiguationData":[OSD([sQuery(id+"F6.wireOp",EDGE,"E19")])]})});
            var sketch = newSketch(context, id + "F36", { "sketchPlane" : qUnion([Q0])});
            skLineSegment(sketch, "E124.bottom", {"start": v(-37.5, 114.2) * mm, "end": v(-35, 114.2) * mm});
            skLineSegment(sketch, "E124.top", {"start": v(-37.5, 114.95) * mm, "end": v(-35, 114.95) * mm});
            skLineSegment(sketch, "E124.left", {"start": v(-37.5, 114.2) * mm, "end": v(-37.5, 114.95) * mm});
            skLineSegment(sketch, "E124.right", {"start": v(-35, 114.2) * mm, "end": v(-35, 114.95) * mm});
            skSolve(sketch);
        }
        {
            var Q0;
            Q0 = qSketchRegion(id + "F36", true);
            extrude(context, id + "F37", {"entities" : qUnion([Q0]), "operationType" : NewBodyOperationType.REMOVE, "oppositeDirection" : true, "depth" : 25 * mm});
        }
        {
            var Q0;
            Q0=makeQuery(id+"F7.boolean.opBoolean","COPY",FACE,{"derivedFrom":makeQuery(id+"F7.opExtrude","SWEPT_FACE",FACE,{"disambiguationData":[OSD([sQuery(id+"F6.wireOp",EDGE,"E21")])]})});
            var sketch = newSketch(context, id + "F38", { "sketchPlane" : qUnion([Q0])});
            skLineSegment(sketch, "E125.bottom", {"start": v(37.5, 114.2) * mm, "end": v(35, 114.2) * mm});
            skLineSegment(sketch, "E125.top", {"start": v(37.5, 114.95) * mm, "end": v(35, 114.95) * mm});
            skLineSegment(sketch, "E125.left", {"start": v(37.5, 114.2) * mm, "end": v(37.5, 114.95) * mm});
            skLineSegment(sketch, "E125.right", {"start": v(35, 114.2) * mm, "end": v(35, 114.95) * mm});
            skSolve(sketch);
        }
        {
            var Q0;
            Q0 = qSketchRegion(id + "F38", true);
            extrude(context, id + "F39", {"entities" : qUnion([Q0]), "operationType" : NewBodyOperationType.REMOVE, "oppositeDirection" : true, "depth" : 25 * mm});
        }
        {
            var Q0;
            Q0=makeQuery(id+"F1.opExtrude","CAP_FACE",FACE,{"disambiguationData":[OSD([sQuery(id+"F0.wireOp",EDGE,"E3")])],"isStart":false});
            var sketch = newSketch(context, id + "F40", { "sketchPlane" : qUnion([Q0])});
            skLineSegment(sketch, "E126", {"start": v(-75, -3.38) * mm, "end": v(-75, -37.5) * mm});
            skLineSegment(sketch, "E127", {"start": v(-106.11, -3.38) * mm, "end": v(-43.89, -3.38) * mm});
            skEllipticalArc(sketch, "E128.0", {});
            skPoint(sketch, "E129.orphan", {"position": v(-150, -37.5) * mm});
            skPoint(sketch, "E130.orphan", {"position": v(0, -37.5) * mm});
            skPoint(sketch, "E131.orphan", {"position": v(-75, 0) * mm});
            const initialGuessF40  = {"E128.0": [-0.075, -0.0375, 1, 0, 0.075, 0.0375, 1.1430642252800542, 1.9985284283097393]};
            skSetInitialGuess(sketch, initialGuessF40);
            skSolve(sketch);
        }
        {
            var Q0;
            {var subQ2=sQuery(id+"F40.wireOp",EDGE,"E128.0");Q0=makeQuery(id+"F40.imprint","IMPRINT",FACE,{"disambiguationData":[TD([[makeQuery(id+"F40.imprint","IMPRINT",EDGE,{"derivedFrom":subQ2}),1.0]])]});}
            extrude(context, id + "F41", {"entities" : qUnion([Q0]), "operationType" : NewBodyOperationType.REMOVE, "oppositeDirection" : true, "depth" : 152 * mm});
        }
        {
            var Q0;
            Q0=makeQuery(id+"F1.opExtrude","CAP_FACE",FACE,{"disambiguationData":[OSD([sQuery(id+"F0.wireOp",EDGE,"E3")])],"isStart":false});
            var sketch = newSketch(context, id + "F42", { "sketchPlane" : qUnion([Q0])});
            skLineSegment(sketch, "E132", {"start": v(-75, -37.5) * mm, "end": v(-75, -17.5) * mm});
            skLineSegment(sketch, "E133", {"start": v(-75, -17.5) * mm, "end": v(-65, -17.5) * mm});
            skLineSegment(sketch, "E134", {"start": v(-65, -17.5) * mm, "end": v(-65, -37.5) * mm});
            skLineSegment(sketch, "E135", {"start": v(-75, -17.5) * mm, "end": v(-85, -17.5) * mm});
            skLineSegment(sketch, "E136", {"start": v(-85, -17.5) * mm, "end": v(-85, -37.5) * mm});
            skLineSegment(sketch, "E137", {"start": v(-85, -37.5) * mm, "end": v(-65, -37.5) * mm});
            skLineSegment(sketch, "E138", {"start": v(-65, -17.5) * mm, "end": v(-65, -9.85) * mm});
            skLineSegment(sketch, "E139", {"start": v(-85, -17.5) * mm, "end": v(-85, -9.85) * mm});
            skLineSegment(sketch, "E140", {"start": v(-85, -9.85) * mm, "end": v(-65, -9.85) * mm});
            skCircle(sketch, "E141", {"center": v(-80, -13.67) * mm, "radius": 1.4 * mm});
            skCircle(sketch, "E142", {"center": v(-70, -13.67) * mm, "radius": 1.4 * mm});
            skLineSegment(sketch, "E143", {"start": v(-80, -13.67) * mm, "end": v(-70, -13.67) * mm, "construction": true});
            skSolve(sketch);
        }
        {
            var Q0;
            {var subQ0=sQuery(id+"F42.wireOp",EDGE,"E132");Q0=makeQuery(id+"F42.imprint","IMPRINT",FACE,{"disambiguationData":[TD([[makeQuery(id+"F42.imprint","IMPRINT",EDGE,{"derivedFrom":subQ0}),-1.0]])]});}
            var Q1;
            {var subQ0=sQuery(id+"F42.wireOp",EDGE,"E132");Q1=makeQuery(id+"F42.imprint","IMPRINT",FACE,{"disambiguationData":[TD([[makeQuery(id+"F42.imprint","IMPRINT",EDGE,{"derivedFrom":subQ0}),1.0]])]});}
            extrude(context, id + "F43", {"entities" : qUnion([Q0, Q1]), "operationType" : NewBodyOperationType.REMOVE, "oppositeDirection" : true, "depth" : 30 * mm});
        }
        {
            var Q0;
            Q0=makeQuery(id+"F42.imprint","IMPRINT",FACE,{"disambiguationData":[TD([[makeQuery(id+"F42.imprint","IMPRINT",EDGE,{"derivedFrom":sQuery(id+"F42.wireOp",EDGE,"E142")}),1.0]])]});
            var Q1;
            Q1=makeQuery(id+"F42.imprint","IMPRINT",FACE,{"disambiguationData":[TD([[makeQuery(id+"F42.imprint","IMPRINT",EDGE,{"derivedFrom":sQuery(id+"F42.wireOp",EDGE,"E141")}),1.0]])]});
            extrude(context, id + "F44", {"entities" : qUnion([Q0, Q1]), "operationType" : NewBodyOperationType.REMOVE, "oppositeDirection" : true, "depth" : 10 * mm});
        }
        {
            var Q0;
            Q0=makeQuery(id+"F41.boolean.opBoolean","COPY",FACE,{"derivedFrom":makeQuery(id+"F41.opExtrude","SWEPT_FACE",FACE,{"disambiguationData":[OSD([sQuery(id+"F40.wireOp",EDGE,"E127")])]})});
            var sketch = newSketch(context, id + "F45", { "sketchPlane" : qUnion([Q0])});
            skPoint(sketch, "E144", {"position": v(43.89, 62.5) * mm});
            skPoint(sketch, "E145", {"position": v(106.11, 62.5) * mm});
            skLineSegment(sketch, "E146", {"start": v(106.11, 62.5) * mm, "end": v(43.89, 62.5) * mm, "construction": true});
            skPoint(sketch, "E147", {"position": v(75, 62.5) * mm});
            skLineSegment(sketch, "E148.bottom", {"start": v(106.11, 93.61) * mm, "end": v(43.89, 93.61) * mm, "construction": true});
            skLineSegment(sketch, "E148.top", {"start": v(106.11, 31.39) * mm, "end": v(43.89, 31.39) * mm, "construction": true});
            skLineSegment(sketch, "E148.left", {"start": v(106.11, 93.61) * mm, "end": v(106.11, 31.39) * mm, "construction": true});
            skLineSegment(sketch, "E148.right", {"start": v(43.89, 93.61) * mm, "end": v(43.89, 31.39) * mm, "construction": true});
            skLineSegment(sketch, "E149", {"start": v(43.89, 82.2) * mm, "end": v(106.11, 82.2) * mm, "construction": true});
            skLineSegment(sketch, "E150", {"start": v(95.61, 33.52) * mm, "end": v(43.89, 33.52) * mm, "construction": true});
            skLineSegment(sketch, "E151", {"start": v(61.44, 75.4) * mm, "end": v(89.17, 75.4) * mm});
            skLineSegment(sketch, "E152", {"start": v(106.11, 62.5) * mm, "end": v(106.11, 33.52) * mm});
            skLineSegment(sketch, "E153", {"start": v(106.11, 48.01) * mm, "end": v(43.89, 48.01) * mm, "construction": true});
            skLineSegment(sketch, "E154", {"start": v(62.96, 62.5) * mm, "end": v(55.89, 48.01) * mm});
            skLineSegment(sketch, "E155", {"start": v(66.33, 69.4) * mm, "end": v(54.33, 69.4) * mm});
            skLineSegment(sketch, "E156", {"start": v(54.33, 69.4) * mm, "end": v(89.17, 69.4) * mm});
            skLineSegment(sketch, "E157", {"start": v(89.17, 75.4) * mm, "end": v(89.17, 69.4) * mm, "construction": true});
            skLineSegment(sketch, "E158", {"start": v(89.17, 62.5) * mm, "end": v(82.46, 62.5) * mm});
            skLineSegment(sketch, "E159", {"start": v(55.89, 82.2) * mm, "end": v(89.17, 82.2) * mm});
            skLineSegment(sketch, "E160", {"start": v(89.17, 82.2) * mm, "end": v(89.17, 62.5) * mm, "construction": true});
            skArc(sketch, "E161", {"start": v(89.17, 62.5) * mm, "mid": v(99.02, 72.35) * mm, "end": v(89.17, 82.2) * mm});
            skArc(sketch, "E162", {"start": v(89.17, 69.4) * mm, "mid": v(92.17, 72.4) * mm, "end": v(89.17, 75.4) * mm});
            skLineSegment(sketch, "E163.trimOffspring", {"start": v(82.46, 62.5) * mm, "end": v(103.33, 36.93) * mm});
            skLineSegment(sketch, "E164.trimOffspring", {"start": v(54.33, 69.4) * mm, "end": v(43.89, 48.01) * mm});
            skLineSegment(sketch, "E165.trimOffspring", {"start": v(71.96, 62.5) * mm, "end": v(92.83, 36.93) * mm});
            skLineSegment(sketch, "E166.trimOffspring", {"start": v(71.96, 62.5) * mm, "end": v(62.96, 62.5) * mm});
            skLineSegment(sketch, "E167", {"start": v(43.89, 48.01) * mm, "end": v(55.89, 48.01) * mm});
            skLineSegment(sketch, "E168", {"start": v(103.33, 36.93) * mm, "end": v(92.83, 36.93) * mm});
            skLineSegment(sketch, "E169", {"start": v(61.44, 75.4) * mm, "end": v(56.64, 75.4) * mm});
            skLineSegment(sketch, "E170", {"start": v(56.64, 75.4) * mm, "end": v(51.1, 82.2) * mm});
            skLineSegment(sketch, "E171", {"start": v(51.1, 82.2) * mm, "end": v(55.89, 82.2) * mm});
            skLineSegment(sketch, "E172", {"start": v(54.78, 80.45) * mm, "end": v(57.47, 77.15) * mm});
            skLineSegment(sketch, "E173", {"start": v(57.47, 77.15) * mm, "end": v(89.17, 77.15) * mm});
            skLineSegment(sketch, "E174", {"start": v(54.78, 80.45) * mm, "end": v(89.17, 80.45) * mm});
            skLineSegment(sketch, "E175", {"start": v(55.43, 67.65) * mm, "end": v(46.7, 49.76) * mm});
            skLineSegment(sketch, "E176", {"start": v(46.7, 49.76) * mm, "end": v(54.8, 49.76) * mm});
            skLineSegment(sketch, "E177", {"start": v(54.8, 49.76) * mm, "end": v(61.87, 64.25) * mm});
            skLineSegment(sketch, "E178", {"start": v(61.87, 64.25) * mm, "end": v(72.8, 64.25) * mm});
            skLineSegment(sketch, "E179", {"start": v(55.43, 67.65) * mm, "end": v(89.17, 67.65) * mm});
            skLineSegment(sketch, "E180", {"start": v(72.8, 64.25) * mm, "end": v(93.66, 38.68) * mm});
            skLineSegment(sketch, "E181", {"start": v(93.66, 38.68) * mm, "end": v(99.65, 38.68) * mm});
            skLineSegment(sketch, "E182", {"start": v(99.65, 38.68) * mm, "end": v(78.78, 64.25) * mm});
            skLineSegment(sketch, "E183.trimOffspring", {"start": v(78.78, 64.25) * mm, "end": v(89.17, 64.25) * mm});
            skArc(sketch, "E184", {"start": v(89.17, 67.65) * mm, "mid": v(93.92, 72.4) * mm, "end": v(89.17, 77.15) * mm});
            skArc(sketch, "E185", {"start": v(89.17, 64.25) * mm, "mid": v(97.27, 72.35) * mm, "end": v(89.17, 80.45) * mm});
            skSolve(sketch);
        }
        {
            var Q0;
            Q0 = qSketchRegion(id + "F45", true);
            extrude(context, id + "F46", {"entities" : qUnion([Q0]), "operationType" : NewBodyOperationType.REMOVE, "oppositeDirection" : true, "depth" : 3 * mm});
        }
    });
